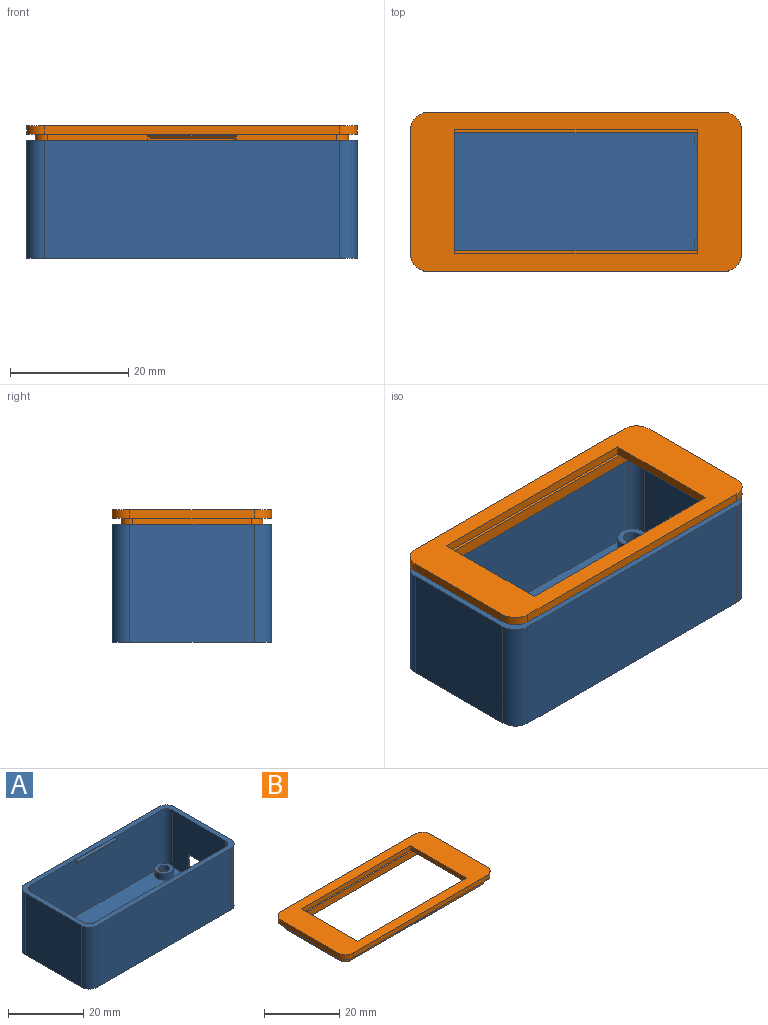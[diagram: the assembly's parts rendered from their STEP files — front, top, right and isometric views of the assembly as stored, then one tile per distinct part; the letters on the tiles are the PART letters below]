
ASSEMBLY  parts=2 mates=1
PART A: 58 faces, bbox 56.2x27x20 mm
  f0: plane 21x20mm, normal (1,0,0), area 281.5mm2, adj f6,f10,f28,f29,f30,f31,f32,f33
  f1: plane 8x0.5mm, normal (0,0,1), area 4mm2, adj f2,f4,f5,f27
  f2: plane 4x0.5mm, normal (0,1,0), area 2mm2, adj f1,f3,f5,f27
  f3: plane 8x0.5mm, normal (0,0,-1), area 4mm2, adj f2,f4,f5,f27
  f4: plane 4x0.5mm, normal (0,-1,0), area 2mm2, adj f1,f3,f5,f27
  f5: plane 20x18.5mm, normal (-1,0,0), area 338mm2, adj f1,f2,f3,f4,f6,f14,f44,f45
  f6: plane 56x27mm, normal (0,0,1), area 235.7mm2, adj f0,f5,f7,f8,f9,f11,f12,f13
  f7: plane 50x20mm, normal (0,1,0), area 1000mm2, adj f6,f10,f40,f41
  f8: plane 21x20mm, normal (-1,0,0), area 420mm2, adj f6,f10,f41,f42
  f9: plane 50x20mm, normal (0,-1,0), area 1000mm2, adj f6,f10,f42,f43
  f10: plane 56x27mm, normal (0,0,-1), area 1350.3mm2, adj f0,f7,f8,f9,f36,f37,f38,f39
  f11: plane 49x18.5mm, normal (0,1,0), area 884mm2, adj f6,f14,f44,f47,f54,f55,f56,f57
  f12: plane 49x18.5mm, normal (0,-1,0), area 884mm2, adj f6,f14,f45,f46,f49,f50,f51,f52
  f13: plane 20x18.5mm, normal (1,0,0), area 370mm2, adj f6,f14,f46,f47
  f14: plane 53x24mm, normal (0,0,1), area 1190mm2, adj f5,f11,f12,f13,f16,f19,f22,f25
  f15: cylinder r=1.5mm len=3mm, axis (0,0,-1), area 14.1mm2, adj f17,f37
  f16: cylinder r=2.5mm len=5mm, axis (0,0,-1), area 31.4mm2, adj f14,f17
  f17: plane 5x5mm, normal (0,0,1), area 12.6mm2, adj f15,f16
  f18: cylinder r=1.5mm len=3mm, axis (0,0,-1), area 14.1mm2, adj f20,f36
  f19: cylinder r=2.5mm len=5mm, axis (0,0,-1), area 31.4mm2, adj f14,f20
  f20: plane 5x5mm, normal (0,0,1), area 12.6mm2, adj f18,f19
  f21: cylinder r=1.5mm len=3mm, axis (0,0,-1), area 14.1mm2, adj f23,f39
  f22: cylinder r=2.5mm len=5mm, axis (0,0,-1), area 31.4mm2, adj f14,f23
  f23: plane 5x5mm, normal (0,0,1), area 12.6mm2, adj f21,f22
  f24: cylinder r=1.5mm len=3mm, axis (0,0,-1), area 14.1mm2, adj f26,f38
  f25: cylinder r=2.5mm len=5mm, axis (0,0,-1), area 31.4mm2, adj f14,f26
  f26: plane 5x5mm, normal (0,0,1), area 12.6mm2, adj f24,f25
  f27: plane 12x8mm, normal (1,0,0), area 62.5mm2, adj f1,f2,f3,f4,f28,f29,f30,f31
  f28: plane 7.17x1mm, normal (0.71,-0.71,0), area 8.7mm2, adj f0,f27,f32,f33
  f29: plane 11.17x1mm, normal (0.71,0,-0.71), area 14.4mm2, adj f0,f27,f32,f34
  f30: plane 11.17x1mm, normal (0.71,0,0.71), area 14.4mm2, adj f0,f27,f33,f35
  f31: plane 7.17x1mm, normal (0.71,0.71,0), area 8.7mm2, adj f0,f27,f34,f35
  f32: cylinder r=2mm len=2.63mm, axis (-0.58,-0.58,-0.58), area 3.6mm2, adj f0,f27,f28,f29
  f33: cylinder r=2mm len=2.63mm, axis (0.58,0.58,-0.58), area 3.6mm2, adj f0,f27,f28,f30
  f34: cylinder r=2mm len=2.63mm, axis (0.58,-0.58,0.58), area 3.6mm2, adj f0,f27,f29,f31
  f35: cylinder r=2mm len=2.63mm, axis (-0.58,0.58,0.58), area 3.6mm2, adj f0,f27,f30,f31
  f36: cone r=1.5mm half-angle=45deg, axis (0,0,-1), area 44.4mm2, adj f10,f18
  f37: cone r=1.5mm half-angle=45deg, axis (0,0,-1), area 44.4mm2, adj f10,f15
  f38: cone r=1.5mm half-angle=45deg, axis (0,0,-1), area 44.4mm2, adj f10,f24
  f39: cone r=1.5mm half-angle=45deg, axis (0,0,-1), area 44.4mm2, adj f10,f21
  f40: cylinder r=3mm len=20mm, axis (0,0,1), area 94.2mm2, adj f0,f6,f7,f10
  f41: cylinder r=3mm len=20mm, axis (0,0,-1), area 94.2mm2, adj f6,f7,f8,f10
  f42: cylinder r=3mm len=20mm, axis (0,0,1), area 94.2mm2, adj f6,f8,f9,f10
  f43: cylinder r=3mm len=20mm, axis (0,0,-1), area 94.2mm2, adj f0,f6,f9,f10
  f44: cylinder r=2mm len=18.5mm, axis (0,0,1), area 58.1mm2, adj f5,f6,f11,f14
  f45: cylinder r=2mm len=18.5mm, axis (0,0,-1), area 58.1mm2, adj f5,f6,f12,f14
  f46: cylinder r=2mm len=18.5mm, axis (0,0,1), area 58.1mm2, adj f6,f12,f13,f14
  f47: cylinder r=2mm len=18.5mm, axis (0,0,-1), area 58.1mm2, adj f6,f11,f13,f14
  f48: plane 14x0.5mm, normal (0,-1,0), area 7mm2, adj f49,f50,f51,f52
  f49: plane 1.5x0.5mm, normal (-0.71,-0.71,0), area 0.7mm2, adj f12,f48,f50,f51
  f50: plane 15x0.5mm, normal (0,-0.71,-0.71), area 10.3mm2, adj f12,f48,f49,f52
  f51: plane 15x0.5mm, normal (0,-0.71,0.71), area 10.3mm2, adj f12,f48,f49,f52
  f52: plane 1.5x0.5mm, normal (0.71,-0.71,0), area 0.7mm2, adj f12,f48,f50,f51
  f53: plane 14x0.5mm, normal (0,1,0), area 7mm2, adj f54,f55,f56,f57
  f54: plane 1.5x0.5mm, normal (0.71,0.71,0), area 0.7mm2, adj f11,f53,f55,f56
  f55: plane 15x0.5mm, normal (0,0.71,-0.71), area 10.3mm2, adj f11,f53,f54,f57
  f56: plane 15x0.5mm, normal (0,0.71,0.71), area 10.3mm2, adj f11,f53,f54,f57
  f57: plane 1.5x0.5mm, normal (-0.71,0.71,0), area 0.7mm2, adj f11,f53,f55,f56
PART B: 41 faces, bbox 56x27x3.5 mm
  f0: plane 49x2mm, normal (0,1,0), area 75.5mm2, adj f3,f4,f27,f28,f37,f38,f39,f40
  f1: plane 49x2mm, normal (0,-1,0), area 75.5mm2, adj f3,f4,f29,f30,f32,f33,f34,f35
  f2: plane 41x0.5mm, normal (0,0,1), area 20.5mm2, adj f11,f12,f13,f23
  f3: plane 53x24mm, normal (0,0,-1), area 288.6mm2, adj f0,f1,f18,f19,f22,f23,f24,f25
  f4: plane 56x27mm, normal (0,0,-1), area 235.7mm2, adj f0,f1,f6,f7,f8,f9,f14,f15
  f5: plane 56x27mm, normal (0,0,1), area 643.3mm2, adj f6,f7,f8,f9,f10,f11,f12,f13
  f6: plane 50x1.5mm, normal (0,-1,0), area 75mm2, adj f4,f5,f14,f17
  f7: plane 21x1.5mm, normal (1,0,0), area 31.5mm2, adj f4,f5,f14,f15
  f8: plane 50x1.5mm, normal (0,1,0), area 75mm2, adj f4,f5,f15,f16
  f9: plane 21x1.5mm, normal (-1,0,0), area 31.5mm2, adj f4,f5,f16,f17
  f10: plane 41x1.5mm, normal (0,1,0), area 61.5mm2, adj f5,f11,f13,f20
  f11: plane 21x1.5mm, normal (-1,0,0), area 31.5mm2, adj f2,f5,f10,f12,f20,f21
  f12: plane 41x1.5mm, normal (0,-1,0), area 61.5mm2, adj f2,f5,f11,f13
  f13: plane 21x1.5mm, normal (1,0,0), area 31.5mm2, adj f2,f5,f10,f12,f20,f26
  f14: cylinder r=3mm len=3mm, axis (0,0,1), area 7.1mm2, adj f4,f5,f6,f7
  f15: cylinder r=3mm len=3mm, axis (0,0,-1), area 7.1mm2, adj f4,f5,f7,f8
  f16: cylinder r=3mm len=3mm, axis (0,0,1), area 7.1mm2, adj f4,f5,f8,f9
  f17: cylinder r=3mm len=3mm, axis (0,0,-1), area 7.1mm2, adj f4,f5,f6,f9
  f18: plane 20x2mm, normal (-1,0,0), area 40mm2, adj f3,f4,f28,f29
  f19: plane 20x2mm, normal (1,0,0), area 40mm2, adj f3,f4,f27,f30
  f20: plane 41x0.5mm, normal (0,0,1), area 20.5mm2, adj f10,f11,f13,f25
  f21: plane 20x4mm, normal (0,0,-1), area 80mm2, adj f11,f23,f24,f25
  f22: plane 20x2mm, normal (1,0,0), area 40mm2, adj f3,f23,f25,f26
  f23: plane 49x2mm, normal (0,-1,0), area 98mm2, adj f2,f3,f21,f22,f24,f26
  f24: plane 20x2mm, normal (-1,0,0), area 40mm2, adj f3,f21,f23,f25
  f25: plane 49x2mm, normal (0,1,0), area 98mm2, adj f3,f20,f21,f22,f24,f26
  f26: plane 20x4mm, normal (0,0,-1), area 80mm2, adj f13,f22,f23,f25
  f27: cylinder r=2mm len=2mm, axis (0,0,-1), area 6.3mm2, adj f0,f3,f4,f19
  f28: cylinder r=2mm len=2mm, axis (0,0,1), area 6.3mm2, adj f0,f3,f4,f18
  f29: cylinder r=2mm len=2mm, axis (0,0,-1), area 6.3mm2, adj f1,f3,f4,f18
  f30: cylinder r=2mm len=2mm, axis (0,0,1), area 6.3mm2, adj f1,f3,f4,f19
  f31: plane 14x0.5mm, normal (0,-1,0), area 7mm2, adj f32,f33,f34,f35
  f32: plane 1.5x0.5mm, normal (-0.71,-0.71,0), area 0.7mm2, adj f1,f31,f33,f34
  f33: plane 15x0.5mm, normal (0,-0.71,0.71), area 10.3mm2, adj f1,f31,f32,f35
  f34: plane 15x0.5mm, normal (0,-0.71,-0.71), area 10.3mm2, adj f1,f31,f32,f35
  f35: plane 1.5x0.5mm, normal (0.71,-0.71,0), area 0.7mm2, adj f1,f31,f33,f34
  f36: plane 14x0.5mm, normal (0,1,0), area 7mm2, adj f37,f38,f39,f40
  f37: plane 1.5x0.5mm, normal (0.71,0.71,0), area 0.7mm2, adj f0,f36,f38,f39
  f38: plane 15x0.5mm, normal (0,0.71,-0.71), area 10.3mm2, adj f0,f36,f37,f40
  f39: plane 15x0.5mm, normal (0,0.71,0.71), area 10.3mm2, adj f0,f36,f37,f40
  f40: plane 1.5x0.5mm, normal (-0.71,0.71,0), area 0.7mm2, adj f0,f36,f38,f39
PLACE A t=(0.94,-45.01,7.67)mm fixed
PLACE B t=(0.94,-96.18,28.67)mm
MATE slider B.f4 <-> A.f6  axis (0,0,-1) through (-24.06,-31.51,28.67)mm
